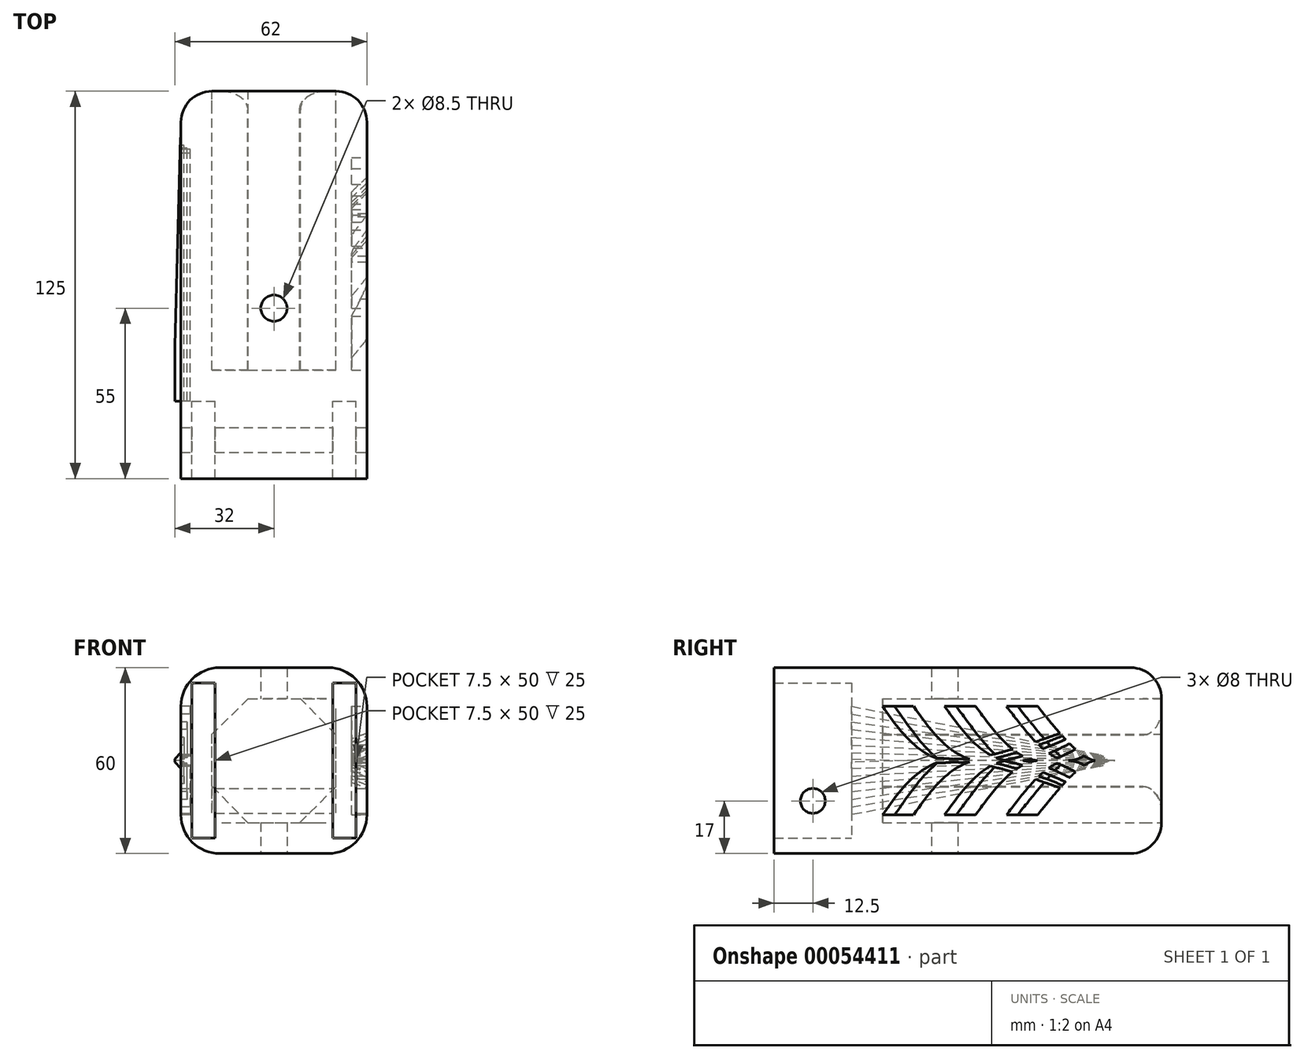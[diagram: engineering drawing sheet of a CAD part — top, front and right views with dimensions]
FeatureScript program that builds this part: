
annotation { "Feature Type Name" : "Feature", "Feature Type Description" : "" }
export const myFeature = defineFeature(function(context is Context, id is Id, definition is map)
    precondition{}
    {
        {
            var Q0;
            Q0=qCreatedBy(makeId("Front.planeOp"),FACE);
            var sketch = newSketch(context, id + "F0", { "sketchPlane" : qUnion([Q0])});
            skLineSegment(sketch, "E0.bottom", {"start": v(-30, 30) * mm, "end": v(30, 30) * mm});
            skLineSegment(sketch, "E0.top", {"start": v(-30, -30) * mm, "end": v(30, -30) * mm});
            skLineSegment(sketch, "E0.left", {"start": v(-30, 30) * mm, "end": v(-30, -30) * mm});
            skLineSegment(sketch, "E0.right", {"start": v(30, 30) * mm, "end": v(30, -30) * mm});
            skPoint(sketch, "E1", {"position": v(-26.5, -30) * mm});
            skPoint(sketch, "E2", {"position": v(-19, -30) * mm});
            skPoint(sketch, "E3", {"position": v(19, -30) * mm});
            skPoint(sketch, "E4", {"position": v(30, -25) * mm});
            skPoint(sketch, "E5", {"position": v(30, 25) * mm});
            skPoint(sketch, "E6", {"position": v(0, 30) * mm});
            skPoint(sketch, "E7", {"position": v(0, -30) * mm});
            skPoint(sketch, "E8", {"position": v(26.5, -30) * mm});
            skPoint(sketch, "E9", {"position": v(30, 0) * mm});
            skLineSegment(sketch, "E10", {"start": v(-26.5, -30) * mm, "end": v(-26.5, 30) * mm, "construction": true});
            skLineSegment(sketch, "E11", {"start": v(-19, -30) * mm, "end": v(-19, 30) * mm, "construction": true});
            skLineSegment(sketch, "E12", {"start": v(19, -30) * mm, "end": v(19, 30) * mm, "construction": true});
            skLineSegment(sketch, "E13", {"start": v(26.5, -30) * mm, "end": v(26.5, 30) * mm, "construction": true});
            skLineSegment(sketch, "E14", {"start": v(30, -25) * mm, "end": v(-30, -25) * mm, "construction": true});
            skLineSegment(sketch, "E15", {"start": v(30, 25) * mm, "end": v(-30, 25) * mm, "construction": true});
            skPoint(sketch, "E16", {"position": v(-26.5, 25) * mm});
            skPoint(sketch, "E17", {"position": v(-19, 25) * mm});
            skPoint(sketch, "E18", {"position": v(-26.5, -25) * mm});
            skPoint(sketch, "E19", {"position": v(-19, -25) * mm});
            skPoint(sketch, "E20", {"position": v(19, -25) * mm});
            skPoint(sketch, "E21", {"position": v(26.5, -25) * mm});
            skPoint(sketch, "E22", {"position": v(26.5, 25) * mm});
            skPoint(sketch, "E23", {"position": v(19, 25) * mm});
            skLineSegment(sketch, "E24", {"start": v(-26.5, 25) * mm, "end": v(-19, 25) * mm});
            skLineSegment(sketch, "E25", {"start": v(-26.5, 25) * mm, "end": v(-26.5, -25) * mm});
            skLineSegment(sketch, "E26", {"start": v(-26.5, -25) * mm, "end": v(-19, -25) * mm});
            skLineSegment(sketch, "E27", {"start": v(19, 25) * mm, "end": v(19, -25) * mm});
            skLineSegment(sketch, "E28", {"start": v(19, -25) * mm, "end": v(26.5, -25) * mm});
            skLineSegment(sketch, "E29", {"start": v(-19, 25) * mm, "end": v(-19, -25) * mm});
            skLineSegment(sketch, "E30", {"start": v(19, 25) * mm, "end": v(26.5, 25) * mm});
            skLineSegment(sketch, "E31", {"start": v(26.5, 25) * mm, "end": v(26.5, -25) * mm});
            skSolve(sketch);
        }
        {
            var Q0;
            Q0=makeQuery(id+"F0.imprint","IMPRINT",FACE,{"disambiguationData":[TD([[makeQuery(id+"F0.imprint","IMPRINT",EDGE,{"derivedFrom":sQuery(id+"F0.wireOp",EDGE,"E0.bottom")}),-1.0]])]});
            extrude(context, id + "F1", {"entities" : qUnion([Q0]), "depth" : 25 * mm});
        }
        {
            var Q0;
            Q0=makeQuery(id+"F1.opExtrude","SWEPT_FACE",FACE,{"disambiguationData":[OSD([sQuery(id+"F0.wireOp",EDGE,"E0.right")])]});
            var sketch = newSketch(context, id + "F2", { "sketchPlane" : qUnion([Q0])});
            skPoint(sketch, "E32", {"position": v(-12.5, -13) * mm});
            skSolve(sketch);
        }
        {
            var Q0;
            Q0=sQuery(id+"F2.wireOp",VERTEX,"E32");
            var Q1;
            Q1=makeQuery(id+"F1.opExtrude","SWEPT_BODY",BODY,{"disambiguationData":[OSD([sQuery(id+"F0.wireOp",EDGE,"E0.bottom"),sQuery(id+"F0.wireOp",EDGE,"E0.top"),sQuery(id+"F0.wireOp",EDGE,"E0.left"),sQuery(id+"F0.wireOp",EDGE,"E0.right"),sQuery(id+"F0.wireOp",EDGE,"E24"),sQuery(id+"F0.wireOp",EDGE,"E25"),sQuery(id+"F0.wireOp",EDGE,"E26"),sQuery(id+"F0.wireOp",EDGE,"E27"),sQuery(id+"F0.wireOp",EDGE,"E28"),sQuery(id+"F0.wireOp",EDGE,"E29"),sQuery(id+"F0.wireOp",EDGE,"E30"),sQuery(id+"F0.wireOp",EDGE,"E31")])]});
            hole(context, id + "F3", {"style" : HoleStyle.SIMPLE, "holeDiameter" : 8 * mm, "endStyle" : HoleEndStyle.THROUGH, "locations" : qUnion([Q0]), "scope" : qUnion([Q1])});
        }
        {
            var Q0;
            Q0=makeQuery(id+"F1.opExtrude","SWEPT_EDGE",EDGE,{"disambiguationData":[OSD([sQuery(id+"F0.wireOp",EDGE,"E0.bottom"),sQuery(id+"F0.wireOp",EDGE,"E0.left")])]});
            var Q1;
            Q1=makeQuery(id+"F1.opExtrude","SWEPT_EDGE",EDGE,{"disambiguationData":[OSD([sQuery(id+"F0.wireOp",EDGE,"E0.bottom"),sQuery(id+"F0.wireOp",EDGE,"E0.right")])]});
            var Q2;
            Q2=makeQuery(id+"F1.opExtrude","SWEPT_EDGE",EDGE,{"disambiguationData":[OSD([sQuery(id+"F0.wireOp",EDGE,"E0.top"),sQuery(id+"F0.wireOp",EDGE,"E0.left")])]});
            var Q3;
            Q3=makeQuery(id+"F1.opExtrude","SWEPT_EDGE",EDGE,{"disambiguationData":[OSD([sQuery(id+"F0.wireOp",EDGE,"E0.top"),sQuery(id+"F0.wireOp",EDGE,"E0.right")])]});
            fillet(context, id + "F4", {"entities" : qUnion([Q0, Q1, Q2, Q3]), "radius" : 12.5 * mm, "tangentPropagation" : true, "allowEdgeOverflow" : false});
        }
        {
            var Q0;
            Q0=makeQuery(id+"F1.opExtrude","CAP_FACE",FACE,{"disambiguationData":[OSD([sQuery(id+"F0.wireOp",EDGE,"E0.bottom"),sQuery(id+"F0.wireOp",EDGE,"E0.top"),sQuery(id+"F0.wireOp",EDGE,"E0.left"),sQuery(id+"F0.wireOp",EDGE,"E0.right"),sQuery(id+"F0.wireOp",EDGE,"E24"),sQuery(id+"F0.wireOp",EDGE,"E25"),sQuery(id+"F0.wireOp",EDGE,"E26"),sQuery(id+"F0.wireOp",EDGE,"E27"),sQuery(id+"F0.wireOp",EDGE,"E28"),sQuery(id+"F0.wireOp",EDGE,"E29"),sQuery(id+"F0.wireOp",EDGE,"E30"),sQuery(id+"F0.wireOp",EDGE,"E31")])],"isStart":true});
            var sketch = newSketch(context, id + "F5", { "sketchPlane" : qUnion([Q0])});
            skLineSegment(sketch, "E33.bottom", {"start": v(30, -30) * mm, "end": v(-30, -30) * mm});
            skLineSegment(sketch, "E33.top", {"start": v(30, 30) * mm, "end": v(-30, 30) * mm});
            skLineSegment(sketch, "E33.left", {"start": v(30, -30) * mm, "end": v(30, 30) * mm});
            skLineSegment(sketch, "E33.right", {"start": v(-30, -30) * mm, "end": v(-30, 30) * mm});
            skSolve(sketch);
        }
        {
            var Q0;
            Q0 = qSketchRegion(id + "F5", true);
            extrude(context, id + "F6", {"entities" : qUnion([Q0]), "operationType" : NewBodyOperationType.ADD, "depth" : 100 * mm});
        }
        {
            var Q0;
            Q0=makeQuery(id+"F6.opExtrude","SWEPT_EDGE",EDGE,{"disambiguationData":[OSD([sQuery(id+"F5.wireOp",EDGE,"E33.bottom"),sQuery(id+"F5.wireOp",EDGE,"E33.right")])]});
            var Q1;
            Q1=makeQuery(id+"F6.opExtrude","SWEPT_EDGE",EDGE,{"disambiguationData":[OSD([sQuery(id+"F5.wireOp",EDGE,"E33.bottom"),sQuery(id+"F5.wireOp",EDGE,"E33.left")])]});
            var Q2;
            Q2=makeQuery(id+"F6.opExtrude","SWEPT_EDGE",EDGE,{"disambiguationData":[OSD([sQuery(id+"F5.wireOp",EDGE,"E33.top"),sQuery(id+"F5.wireOp",EDGE,"E33.right")])]});
            var Q3;
            Q3=makeQuery(id+"F6.opExtrude","SWEPT_EDGE",EDGE,{"disambiguationData":[OSD([sQuery(id+"F5.wireOp",EDGE,"E33.top"),sQuery(id+"F5.wireOp",EDGE,"E33.left")])]});
            fillet(context, id + "F7", {"entities" : qUnion([Q0, Q1, Q2, Q3]), "radius" : 12.5 * mm, "tangentPropagation" : true, "allowEdgeOverflow" : false});
        }
        {
            var Q0;
            Q0=makeQuery(id+"F6.opExtrude","CAP_FACE",FACE,{"disambiguationData":[OSD([sQuery(id+"F5.wireOp",EDGE,"E33.bottom"),sQuery(id+"F5.wireOp",EDGE,"E33.top"),sQuery(id+"F5.wireOp",EDGE,"E33.left"),sQuery(id+"F5.wireOp",EDGE,"E33.right")])],"isStart":false});
            fillet(context, id + "F8", {"entities" : qUnion([Q0]), "radius" : 10 * mm, "tangentPropagation" : true, "allowEdgeOverflow" : false});
        }
        {
            var Q0;
            Q0=makeQuery(id+"F6.opExtrude","CAP_FACE",FACE,{"disambiguationData":[OSD([sQuery(id+"F5.wireOp",EDGE,"E33.bottom"),sQuery(id+"F5.wireOp",EDGE,"E33.top"),sQuery(id+"F5.wireOp",EDGE,"E33.left"),sQuery(id+"F5.wireOp",EDGE,"E33.right")])],"isStart":false});
            var sketch = newSketch(context, id + "F9", { "sketchPlane" : qUnion([Q0])});
            skPoint(sketch, "E34", {"position": v(0, 0) * mm});
            skCircle(sketch, "E35.cCircle", {"center": v(0, 0) * mm, "radius": 20.07 * mm, "construction": true});
            skLineSegment(sketch, "E35.0", {"start": v(-20.14, 8.14) * mm, "end": v(-8.49, 20) * mm});
            skLineSegment(sketch, "E35.1", {"start": v(-8.49, 20) * mm, "end": v(8.14, 20.14) * mm});
            skLineSegment(sketch, "E35.2", {"start": v(8.14, 20.14) * mm, "end": v(20, 8.49) * mm});
            skLineSegment(sketch, "E35.3", {"start": v(20, 8.49) * mm, "end": v(20.14, -8.14) * mm});
            skLineSegment(sketch, "E35.4", {"start": v(20.14, -8.14) * mm, "end": v(8.49, -20) * mm});
            skLineSegment(sketch, "E35.5", {"start": v(8.49, -20) * mm, "end": v(-8.14, -20.14) * mm});
            skLineSegment(sketch, "E35.6", {"start": v(-8.14, -20.14) * mm, "end": v(-20, -8.49) * mm});
            skLineSegment(sketch, "E35.7", {"start": v(-20, -8.49) * mm, "end": v(-20.14, 8.14) * mm});
            skPoint(sketch, "E35.0.midPoint", {"position": v(-14.31, 14.07) * mm});
            skSolve(sketch);
        }
        {
            var Q0;
            {var subQ1=sQuery(id+"F5.wireOp",EDGE,"E33.right");var subQ2=sQuery(id+"F5.wireOp",EDGE,"E33.left");var subQ3=sQuery(id+"F5.wireOp",EDGE,"E33.top");var subQ4=sQuery(id+"F5.wireOp",EDGE,"E33.bottom");var subQ5=makeQuery(id+"F6.opExtrude","CAP_FACE",FACE,{"disambiguationData":[OSD([subQ4,subQ3,subQ2,subQ1])],"isStart":false});var subQ15=makeQuery(id+"F8.opFillet","BLEND_EDGE",EDGE,{"blendedFrom":[makeQuery(id+"F6.opExtrude","CAP_EDGE",EDGE,{"disambiguationData":[OSD([subQ1])],"isStart":false}),subQ5],"blendedInto":[subQ5]});var subQ18=sQuery(id+"F9.wireOp",EDGE,"E35.0");var subQ20=makeQuery(id+"F9.imprint","INTERSECT",VERTEX,{"derivedFrom":[subQ15,subQ18]});Q0=makeQuery(id+"F9.imprint","IMPRINT",FACE,{"disambiguationData":[TD([[makeQuery(id+"F9.imprint","IMPRINT",EDGE,{"disambiguationData":[TD([[subQ20,-1.0]])],"derivedFrom":subQ18}),-1.0]])]});}
            extrude(context, id + "F10", {"entities" : qUnion([Q0]), "operationType" : NewBodyOperationType.REMOVE, "oppositeDirection" : true, "depth" : 90 * mm});
        }
        {
            var Q0;
            Q0=makeQuery(id+"F10.boolean.opBoolean","COPY",EDGE,{"derivedFrom":makeQuery(id+"F10.opExtrude","CAP_EDGE",EDGE,{"disambiguationData":[OSD([sQuery(id+"F9.wireOp",EDGE,"E35.2")])],"isStart":true})});
            var Q1;
            Q1=makeQuery(id+"F10.boolean.opBoolean","COPY",EDGE,{"derivedFrom":makeQuery(id+"F10.opExtrude","CAP_EDGE",EDGE,{"disambiguationData":[OSD([sQuery(id+"F9.wireOp",EDGE,"E35.4")])],"isStart":true})});
            var Q2;
            Q2=makeQuery(id+"F10.boolean.opBoolean","COPY",EDGE,{"derivedFrom":makeQuery(id+"F10.opExtrude","CAP_EDGE",EDGE,{"disambiguationData":[OSD([sQuery(id+"F9.wireOp",EDGE,"E35.0")])],"isStart":true})});
            var Q3;
            Q3=makeQuery(id+"F10.boolean.opBoolean","COPY",EDGE,{"derivedFrom":makeQuery(id+"F10.opExtrude","CAP_EDGE",EDGE,{"disambiguationData":[OSD([sQuery(id+"F9.wireOp",EDGE,"E35.6")])],"isStart":true})});
            fillet(context, id + "F11", {"entities" : qUnion([Q0, Q1, Q2, Q3]), "radius" : 6 * mm, "tangentPropagation" : true, "allowEdgeOverflow" : false});
        }
        {
            var Q0;
            Q0=makeQuery(id+"F6.boolean.opBoolean","MERGE",FACE,{"derivedFrom":[makeQuery(id+"F1.opExtrude","SWEPT_FACE",FACE,{"disambiguationData":[OSD([sQuery(id+"F0.wireOp",EDGE,"E0.right")])]}),makeQuery(id+"F6.opExtrude","SWEPT_FACE",FACE,{"disambiguationData":[OSD([sQuery(id+"F5.wireOp",EDGE,"E33.right")])]})]});
            var sketch = newSketch(context, id + "F12", { "sketchPlane" : qUnion([Q0])});
            skPoint(sketch, "E36", {"position": v(10, 17.5) * mm});
            skPoint(sketch, "E37", {"position": v(20, 17.5) * mm});
            skPoint(sketch, "E38", {"position": v(30, 17.5) * mm});
            skPoint(sketch, "E39", {"position": v(40, 17.5) * mm});
            skPoint(sketch, "E40", {"position": v(50, 17.5) * mm});
            skPoint(sketch, "E41", {"position": v(60, 17.5) * mm});
            skPoint(sketch, "E42", {"position": v(70, 17.5) * mm});
            skPoint(sketch, "E43", {"position": v(80, 17.5) * mm});
            skPoint(sketch, "E44", {"position": v(10, -17.5) * mm});
            skPoint(sketch, "E45", {"position": v(20, -17.5) * mm});
            skPoint(sketch, "E46", {"position": v(30, -17.5) * mm});
            skPoint(sketch, "E47", {"position": v(40, -17.5) * mm});
            skPoint(sketch, "E48", {"position": v(50, -17.5) * mm});
            skPoint(sketch, "E49", {"position": v(60, -17.5) * mm});
            skPoint(sketch, "E50", {"position": v(70, -17.5) * mm});
            skPoint(sketch, "E51", {"position": v(80, -17.5) * mm});
            skPoint(sketch, "E52", {"position": v(10, 0) * mm});
            skPoint(sketch, "E53", {"position": v(20, 0) * mm});
            skPoint(sketch, "E54", {"position": v(30, 0) * mm});
            skPoint(sketch, "E55", {"position": v(40, 0) * mm});
            skPoint(sketch, "E56", {"position": v(50, 0) * mm});
            skPoint(sketch, "E57", {"position": v(60, 0) * mm});
            skPoint(sketch, "E58", {"position": v(70, 0) * mm});
            skPoint(sketch, "E59", {"position": v(80, 0) * mm});
            skFitSpline(sketch, "E60", {"points": [v(0, 17.5) * mm, v(20, 0) * mm, v(90, 17.5) * mm], "startDerivative": vector(41.71, -60.4) * mm, "endDerivative": vector(131, 51.29) * mm});
            skFitSpline(sketch, "E61", {"points": [v(0, -17.5) * mm, v(20, 0) * mm, v(90, -17.5) * mm], "startDerivative": vector(41.71, 60.4) * mm, "endDerivative": vector(131, -51.29) * mm});
            skFitSpline(sketch, "E62", {"points": [v(10, 17.5) * mm, v(30, 0) * mm, v(90, 17.5) * mm], "startDerivative": vector(41.1, -58.8) * mm, "endDerivative": vector(113.79, 51.08) * mm});
            skFitSpline(sketch, "E63", {"points": [v(20, 17.5) * mm, v(40, 0) * mm, v(90, 17.5) * mm], "startDerivative": vector(40.53, -57.16) * mm, "endDerivative": vector(96.3, 51) * mm});
            skFitSpline(sketch, "E64", {"points": [v(30, 17.5) * mm, v(50, 0) * mm, v(90, 17.5) * mm], "startDerivative": vector(40.03, -55.5) * mm, "endDerivative": vector(78.39, 51.12) * mm});
            skFitSpline(sketch, "E65", {"points": [v(40, 17.5) * mm, v(60, 0) * mm, v(90, 17.5) * mm], "startDerivative": vector(39.74, -53.9) * mm, "endDerivative": vector(59.81, 51.56) * mm});
            skFitSpline(sketch, "E66", {"points": [v(50, 17.5) * mm, v(70, 0) * mm, v(90, 17.5) * mm], "startDerivative": vector(40, -52.5) * mm, "endDerivative": vector(40, 52.5) * mm});
            skFitSpline(sketch, "E67", {"points": [v(60, 17.5) * mm, v(80, 0) * mm, v(90, 17.5) * mm], "startDerivative": vector(41.68, -51.54) * mm, "endDerivative": vector(17.77, 53.96) * mm});
            skFitSpline(sketch, "E68", {"points": [v(10, -17.5) * mm, v(30, 0) * mm, v(90, -17.5) * mm], "startDerivative": vector(41.1, 58.8) * mm, "endDerivative": vector(113.79, -51.08) * mm});
            skFitSpline(sketch, "E69", {"points": [v(20, -17.5) * mm, v(40, 0) * mm, v(90, -17.5) * mm], "startDerivative": vector(40.53, 57.16) * mm, "endDerivative": vector(96.3, -51) * mm});
            skFitSpline(sketch, "E70", {"points": [v(30, -17.5) * mm, v(50, 0) * mm, v(90, -17.5) * mm], "startDerivative": vector(40.03, 55.5) * mm, "endDerivative": vector(78.39, -51.12) * mm});
            skFitSpline(sketch, "E71", {"points": [v(40, -17.5) * mm, v(60, 0) * mm, v(90, -17.5) * mm], "startDerivative": vector(39.74, 53.9) * mm, "endDerivative": vector(59.81, -51.56) * mm});
            skFitSpline(sketch, "E72", {"points": [v(50, -17.5) * mm, v(70, 0) * mm, v(90, -17.5) * mm], "startDerivative": vector(40, 52.5) * mm, "endDerivative": vector(40, -52.5) * mm});
            skFitSpline(sketch, "E73", {"points": [v(60, -17.5) * mm, v(80, 0) * mm, v(90, -17.5) * mm], "startDerivative": vector(41.68, 51.54) * mm, "endDerivative": vector(17.77, -53.96) * mm});
            skSolve(sketch);
        }
        {
            var Q0;
            {var subQ0=sQuery(id+"F12.wireOp",EDGE,"E72");var subQ1=sQuery(id+"F12.wireOp",EDGE,"E61");var subQ2=makeQuery(id+"F12.imprint","INTERSECT",VERTEX,{"derivedFrom":[subQ1,subQ0]});Q0=makeQuery(id+"F12.imprint","IMPRINT",FACE,{"disambiguationData":[TD([[makeQuery(id+"F12.imprint","IMPRINT",EDGE,{"disambiguationData":[TD([[subQ2,-1.0]])],"derivedFrom":subQ1}),-1.0]])]});}
            var Q1;
            {var subQ0=sQuery(id+"F12.wireOp",EDGE,"E70");var subQ1=sQuery(id+"F12.wireOp",EDGE,"E61");var subQ2=makeQuery(id+"F12.imprint","INTERSECT",VERTEX,{"derivedFrom":[subQ1,subQ0]});Q1=makeQuery(id+"F12.imprint","IMPRINT",FACE,{"disambiguationData":[TD([[makeQuery(id+"F12.imprint","IMPRINT",EDGE,{"disambiguationData":[TD([[subQ2,-1.0]])],"derivedFrom":subQ1}),-1.0]])]});}
            var Q2;
            {var subQ6=sQuery(id+"F12.wireOp",EDGE,"E60");var subQ8=sQuery(id+"F12.wireOp",EDGE,"E68");var subQ10=makeQuery(id+"F12.imprint","INTERSECT",VERTEX,{"disambiguationData":[OD(0.0)],"derivedFrom":[subQ6,subQ8]});Q2=makeQuery(id+"F12.imprint","IMPRINT",FACE,{"disambiguationData":[TD([[makeQuery(id+"F12.imprint","IMPRINT",EDGE,{"disambiguationData":[TD([[subQ10,-1.0]])],"derivedFrom":subQ6}),-1.0]])]});}
            var Q3;
            {var subQ1=sQuery(id+"F12.wireOp",EDGE,"E61");var subQ5=sQuery(id+"F12.wireOp",EDGE,"E62");var subQ9=makeQuery(id+"F12.imprint","INTERSECT",VERTEX,{"disambiguationData":[OD(0.0)],"derivedFrom":[subQ1,subQ5]});Q3=makeQuery(id+"F12.imprint","IMPRINT",FACE,{"disambiguationData":[TD([[makeQuery(id+"F12.imprint","IMPRINT",EDGE,{"disambiguationData":[TD([[subQ9,-1.0]])],"derivedFrom":subQ1}),1.0]])]});}
            var Q4;
            {var subQ0=sQuery(id+"F12.wireOp",EDGE,"E64");var subQ1=sQuery(id+"F12.wireOp",EDGE,"E60");var subQ2=makeQuery(id+"F12.imprint","INTERSECT",VERTEX,{"derivedFrom":[subQ1,subQ0]});Q4=makeQuery(id+"F12.imprint","IMPRINT",FACE,{"disambiguationData":[TD([[makeQuery(id+"F12.imprint","IMPRINT",EDGE,{"disambiguationData":[TD([[subQ2,-1.0]])],"derivedFrom":subQ1}),1.0]])]});}
            var Q5;
            {var subQ0=sQuery(id+"F12.wireOp",EDGE,"E66");var subQ1=sQuery(id+"F12.wireOp",EDGE,"E60");var subQ2=makeQuery(id+"F12.imprint","INTERSECT",VERTEX,{"derivedFrom":[subQ1,subQ0]});Q5=makeQuery(id+"F12.imprint","IMPRINT",FACE,{"disambiguationData":[TD([[makeQuery(id+"F12.imprint","IMPRINT",EDGE,{"disambiguationData":[TD([[subQ2,-1.0]])],"derivedFrom":subQ1}),1.0]])]});}
            var Q6;
            {var subQ0=sQuery(id+"F12.wireOp",EDGE,"E64");var subQ1=sQuery(id+"F12.wireOp",EDGE,"E62");var subQ2=makeQuery(id+"F12.imprint","INTERSECT",VERTEX,{"derivedFrom":[subQ1,subQ0]});Q6=makeQuery(id+"F12.imprint","IMPRINT",FACE,{"disambiguationData":[TD([[makeQuery(id+"F12.imprint","IMPRINT",EDGE,{"disambiguationData":[TD([[subQ2,-1.0]])],"derivedFrom":subQ1}),-1.0]])]});}
            var Q7;
            {var subQ0=sQuery(id+"F12.wireOp",EDGE,"E70");var subQ1=sQuery(id+"F12.wireOp",EDGE,"E68");var subQ2=makeQuery(id+"F12.imprint","INTERSECT",VERTEX,{"derivedFrom":[subQ1,subQ0]});Q7=makeQuery(id+"F12.imprint","IMPRINT",FACE,{"disambiguationData":[TD([[makeQuery(id+"F12.imprint","IMPRINT",EDGE,{"disambiguationData":[TD([[subQ2,-1.0]])],"derivedFrom":subQ1}),1.0]])]});}
            var Q8;
            {var subQ0=sQuery(id+"F12.wireOp",EDGE,"E66");var subQ1=sQuery(id+"F12.wireOp",EDGE,"E62");var subQ2=makeQuery(id+"F12.imprint","INTERSECT",VERTEX,{"derivedFrom":[subQ1,subQ0]});Q8=makeQuery(id+"F12.imprint","IMPRINT",FACE,{"disambiguationData":[TD([[makeQuery(id+"F12.imprint","IMPRINT",EDGE,{"disambiguationData":[TD([[subQ2,-1.0]])],"derivedFrom":subQ1}),-1.0]])]});}
            var Q9;
            {var subQ0=sQuery(id+"F12.wireOp",EDGE,"E66");var subQ1=sQuery(id+"F12.wireOp",EDGE,"E64");var subQ2=makeQuery(id+"F12.imprint","INTERSECT",VERTEX,{"derivedFrom":[subQ1,subQ0]});Q9=makeQuery(id+"F12.imprint","IMPRINT",FACE,{"disambiguationData":[TD([[makeQuery(id+"F12.imprint","IMPRINT",EDGE,{"disambiguationData":[TD([[subQ2,-1.0]])],"derivedFrom":subQ1}),-1.0]])]});}
            var Q10;
            {var subQ0=sQuery(id+"F12.wireOp",EDGE,"E72");var subQ1=sQuery(id+"F12.wireOp",EDGE,"E68");var subQ2=makeQuery(id+"F12.imprint","INTERSECT",VERTEX,{"derivedFrom":[subQ1,subQ0]});Q10=makeQuery(id+"F12.imprint","IMPRINT",FACE,{"disambiguationData":[TD([[makeQuery(id+"F12.imprint","IMPRINT",EDGE,{"disambiguationData":[TD([[subQ2,-1.0]])],"derivedFrom":subQ1}),1.0]])]});}
            var Q11;
            {var subQ0=sQuery(id+"F12.wireOp",EDGE,"E72");var subQ1=sQuery(id+"F12.wireOp",EDGE,"E70");var subQ2=makeQuery(id+"F12.imprint","INTERSECT",VERTEX,{"derivedFrom":[subQ1,subQ0]});Q11=makeQuery(id+"F12.imprint","IMPRINT",FACE,{"disambiguationData":[TD([[makeQuery(id+"F12.imprint","IMPRINT",EDGE,{"disambiguationData":[TD([[subQ2,-1.0]])],"derivedFrom":subQ1}),1.0]])]});}
            var Q12;
            {var subQ0=sQuery(id+"F12.wireOp",EDGE,"E70");var subQ1=sQuery(id+"F12.wireOp",EDGE,"E64");var subQ2=makeQuery(id+"F12.imprint","INTERSECT",VERTEX,{"disambiguationData":[OD(1.0)],"derivedFrom":[subQ1,subQ0]});Q12=makeQuery(id+"F12.imprint","IMPRINT",FACE,{"disambiguationData":[TD([[makeQuery(id+"F12.imprint","IMPRINT",EDGE,{"disambiguationData":[TD([[subQ2,-1.0]])],"derivedFrom":subQ1}),-1.0]])]});}
            var Q13;
            {var subQ0=sQuery(id+"F12.wireOp",EDGE,"E72");var subQ1=sQuery(id+"F12.wireOp",EDGE,"E66");var subQ2=makeQuery(id+"F12.imprint","INTERSECT",VERTEX,{"derivedFrom":[subQ1,subQ0]});Q13=makeQuery(id+"F12.imprint","IMPRINT",FACE,{"disambiguationData":[TD([[makeQuery(id+"F12.imprint","IMPRINT",EDGE,{"disambiguationData":[TD([[subQ2,-1.0]])],"derivedFrom":subQ1}),-1.0]])]});}
            extrude(context, id + "F13", {"entities" : qUnion([Q0, Q1, Q2, Q3, Q4, Q5, Q6, Q7, Q8, Q9, Q10, Q11, Q12, Q13]), "operationType" : NewBodyOperationType.REMOVE, "oppositeDirection" : true, "depth" : 5 * mm});
        }
        {
            var Q0;
            Q0=makeQuery(id+"F6.boolean.opBoolean","MERGE",FACE,{"derivedFrom":[makeQuery(id+"F1.opExtrude","SWEPT_FACE",FACE,{"disambiguationData":[OSD([sQuery(id+"F0.wireOp",EDGE,"E0.top")])]}),makeQuery(id+"F6.opExtrude","SWEPT_FACE",FACE,{"disambiguationData":[OSD([sQuery(id+"F5.wireOp",EDGE,"E33.bottom")])]})]});
            var sketch = newSketch(context, id + "F14", { "sketchPlane" : qUnion([Q0])});
            skPoint(sketch, "E74", {"position": v(0, -90) * mm});
            skPoint(sketch, "E75", {"position": v(0, -30) * mm});
            skSolve(sketch);
        }
        {
            var Q0;
            Q0=sQuery(id+"F14.wireOp",VERTEX,"E75");
            var Q1;
            Q1=makeQuery(id+"F1.opExtrude","SWEPT_BODY",BODY,{"disambiguationData":[OSD([sQuery(id+"F0.wireOp",EDGE,"E0.bottom"),sQuery(id+"F0.wireOp",EDGE,"E0.top"),sQuery(id+"F0.wireOp",EDGE,"E0.left"),sQuery(id+"F0.wireOp",EDGE,"E0.right"),sQuery(id+"F0.wireOp",EDGE,"E24"),sQuery(id+"F0.wireOp",EDGE,"E25"),sQuery(id+"F0.wireOp",EDGE,"E26"),sQuery(id+"F0.wireOp",EDGE,"E27"),sQuery(id+"F0.wireOp",EDGE,"E28"),sQuery(id+"F0.wireOp",EDGE,"E29"),sQuery(id+"F0.wireOp",EDGE,"E30"),sQuery(id+"F0.wireOp",EDGE,"E31")])]});
            hole(context, id + "F15", {"style" : HoleStyle.SIMPLE, "holeDiameter" : 8.5 * mm, "endStyle" : HoleEndStyle.THROUGH, "locations" : qUnion([Q0]), "scope" : qUnion([Q1])});
        }
        {
            var Q0;
            {var subQ0=sQuery(id+"F12.wireOp",EDGE,"E67");Q0=makeQuery(id+"F13.boolean.opBoolean","COPY",EDGE,{"derivedFrom":makeQuery(id+"F13.opExtrude","CAP_EDGE",EDGE,{"disambiguationData":[OSD([subQ0]),TDD([makeQuery(id+"F12.imprint","IMPRINT",EDGE,{"disambiguationData":[TD([[makeQuery(id+"F12.imprint","INTERSECT",VERTEX,{"derivedFrom":[sQuery(id+"F12.wireOp",EDGE,"E60"),subQ0]}),1.0]])],"derivedFrom":subQ0})])],"isStart":false})});}
            var Q1;
            {var subQ0=sQuery(id+"F12.wireOp",EDGE,"E67");Q1=makeQuery(id+"F13.boolean.opBoolean","COPY",EDGE,{"derivedFrom":makeQuery(id+"F13.opExtrude","CAP_EDGE",EDGE,{"disambiguationData":[OSD([subQ0]),TDD([makeQuery(id+"F12.imprint","IMPRINT",EDGE,{"disambiguationData":[TD([[makeQuery(id+"F12.imprint","INTERSECT",VERTEX,{"derivedFrom":[sQuery(id+"F12.wireOp",EDGE,"E62"),subQ0]}),-1.0]])],"derivedFrom":subQ0})])],"isStart":false})});}
            var Q2;
            {var subQ0=sQuery(id+"F12.wireOp",EDGE,"E67");Q2=makeQuery(id+"F13.boolean.opBoolean","COPY",EDGE,{"derivedFrom":makeQuery(id+"F13.opExtrude","CAP_EDGE",EDGE,{"disambiguationData":[OSD([subQ0]),TDD([makeQuery(id+"F12.imprint","IMPRINT",EDGE,{"disambiguationData":[TD([[makeQuery(id+"F12.imprint","INTERSECT",VERTEX,{"derivedFrom":[sQuery(id+"F12.wireOp",EDGE,"E64"),subQ0]}),-1.0]])],"derivedFrom":subQ0})])],"isStart":false})});}
            var Q3;
            {var subQ0=sQuery(id+"F12.wireOp",EDGE,"E65");Q3=makeQuery(id+"F13.boolean.opBoolean","COPY",EDGE,{"derivedFrom":makeQuery(id+"F13.opExtrude","CAP_EDGE",EDGE,{"disambiguationData":[OSD([subQ0]),TDD([makeQuery(id+"F12.imprint","IMPRINT",EDGE,{"disambiguationData":[TD([[makeQuery(id+"F12.imprint","INTERSECT",VERTEX,{"derivedFrom":[sQuery(id+"F12.wireOp",EDGE,"E62"),subQ0]}),-1.0]])],"derivedFrom":subQ0})])],"isStart":false})});}
            var Q4;
            {var subQ0=sQuery(id+"F12.wireOp",EDGE,"E65");Q4=makeQuery(id+"F13.boolean.opBoolean","COPY",EDGE,{"derivedFrom":makeQuery(id+"F13.opExtrude","CAP_EDGE",EDGE,{"disambiguationData":[OSD([subQ0]),TDD([makeQuery(id+"F12.imprint","IMPRINT",EDGE,{"disambiguationData":[TD([[makeQuery(id+"F12.imprint","INTERSECT",VERTEX,{"derivedFrom":[sQuery(id+"F12.wireOp",EDGE,"E60"),subQ0]}),1.0]])],"derivedFrom":subQ0})])],"isStart":false})});}
            var Q5;
            {var subQ0=sQuery(id+"F12.wireOp",EDGE,"E73");Q5=makeQuery(id+"F13.boolean.opBoolean","COPY",EDGE,{"derivedFrom":makeQuery(id+"F13.opExtrude","CAP_EDGE",EDGE,{"disambiguationData":[OSD([subQ0]),TDD([makeQuery(id+"F12.imprint","IMPRINT",EDGE,{"disambiguationData":[TD([[makeQuery(id+"F12.imprint","INTERSECT",VERTEX,{"derivedFrom":[sQuery(id+"F12.wireOp",EDGE,"E70"),subQ0]}),-1.0]])],"derivedFrom":subQ0})])],"isStart":false})});}
            var Q6;
            {var subQ0=sQuery(id+"F12.wireOp",EDGE,"E73");Q6=makeQuery(id+"F13.boolean.opBoolean","COPY",EDGE,{"derivedFrom":makeQuery(id+"F13.opExtrude","CAP_EDGE",EDGE,{"disambiguationData":[OSD([subQ0]),TDD([makeQuery(id+"F12.imprint","IMPRINT",EDGE,{"disambiguationData":[TD([[makeQuery(id+"F12.imprint","INTERSECT",VERTEX,{"derivedFrom":[sQuery(id+"F12.wireOp",EDGE,"E68"),subQ0]}),-1.0]])],"derivedFrom":subQ0})])],"isStart":false})});}
            var Q7;
            {var subQ0=sQuery(id+"F12.wireOp",EDGE,"E71");Q7=makeQuery(id+"F13.boolean.opBoolean","COPY",EDGE,{"derivedFrom":makeQuery(id+"F13.opExtrude","CAP_EDGE",EDGE,{"disambiguationData":[OSD([subQ0]),TDD([makeQuery(id+"F12.imprint","IMPRINT",EDGE,{"disambiguationData":[TD([[makeQuery(id+"F12.imprint","INTERSECT",VERTEX,{"derivedFrom":[sQuery(id+"F12.wireOp",EDGE,"E68"),subQ0]}),-1.0]])],"derivedFrom":subQ0})])],"isStart":false})});}
            var Q8;
            {var subQ0=sQuery(id+"F12.wireOp",EDGE,"E73");Q8=makeQuery(id+"F13.boolean.opBoolean","COPY",EDGE,{"derivedFrom":makeQuery(id+"F13.opExtrude","CAP_EDGE",EDGE,{"disambiguationData":[OSD([subQ0]),TDD([makeQuery(id+"F12.imprint","IMPRINT",EDGE,{"disambiguationData":[TD([[makeQuery(id+"F12.imprint","INTERSECT",VERTEX,{"derivedFrom":[sQuery(id+"F12.wireOp",EDGE,"E61"),subQ0]}),1.0]])],"derivedFrom":subQ0})])],"isStart":false})});}
            var Q9;
            {var subQ0=sQuery(id+"F12.wireOp",EDGE,"E71");Q9=makeQuery(id+"F13.boolean.opBoolean","COPY",EDGE,{"derivedFrom":makeQuery(id+"F13.opExtrude","CAP_EDGE",EDGE,{"disambiguationData":[OSD([subQ0]),TDD([makeQuery(id+"F12.imprint","IMPRINT",EDGE,{"disambiguationData":[TD([[makeQuery(id+"F12.imprint","INTERSECT",VERTEX,{"derivedFrom":[sQuery(id+"F12.wireOp",EDGE,"E61"),subQ0]}),1.0]])],"derivedFrom":subQ0})])],"isStart":false})});}
            var Q10;
            {var subQ0=sQuery(id+"F12.wireOp",EDGE,"E63");Q10=makeQuery(id+"F13.boolean.opBoolean","COPY",EDGE,{"derivedFrom":makeQuery(id+"F13.opExtrude","CAP_EDGE",EDGE,{"disambiguationData":[OSD([subQ0]),TDD([makeQuery(id+"F12.imprint","IMPRINT",EDGE,{"disambiguationData":[TD([[makeQuery(id+"F12.imprint","INTERSECT",VERTEX,{"disambiguationData":[OD(0.0)],"derivedFrom":[subQ0,sQuery(id+"F12.wireOp",EDGE,"E68")]}),1.0]])],"derivedFrom":subQ0})])],"isStart":false})});}
            var Q11;
            {var subQ0=sQuery(id+"F12.wireOp",EDGE,"E69");Q11=makeQuery(id+"F13.boolean.opBoolean","COPY",EDGE,{"derivedFrom":makeQuery(id+"F13.opExtrude","CAP_EDGE",EDGE,{"disambiguationData":[OSD([subQ0]),TDD([makeQuery(id+"F12.imprint","IMPRINT",EDGE,{"disambiguationData":[TD([[makeQuery(id+"F12.imprint","INTERSECT",VERTEX,{"disambiguationData":[OD(0.0)],"derivedFrom":[sQuery(id+"F12.wireOp",EDGE,"E62"),subQ0]}),1.0]])],"derivedFrom":subQ0})])],"isStart":false})});}
            chamfer(context, id + "F16", {"entities" : qUnion([Q0, Q1, Q2, Q3, Q4, Q5, Q6, Q7, Q8, Q9, Q10, Q11]), "width" : 5 * mm, "tangentPropagation" : true});
        }
        {
            var Q0;
            Q0=makeQuery(id+"F6.boolean.opBoolean","MERGE",FACE,{"derivedFrom":[makeQuery(id+"F1.opExtrude","SWEPT_FACE",FACE,{"disambiguationData":[OSD([sQuery(id+"F0.wireOp",EDGE,"E0.left")])]}),makeQuery(id+"F6.opExtrude","SWEPT_FACE",FACE,{"disambiguationData":[OSD([sQuery(id+"F5.wireOp",EDGE,"E33.left")])]})]});
            var sketch = newSketch(context, id + "F17", { "sketchPlane" : qUnion([Q0])});
            skPoint(sketch, "E76", {"position": v(-90, 0) * mm});
            skPoint(sketch, "E77", {"position": v(0, 17.5) * mm});
            skPoint(sketch, "E78", {"position": v(0, 12.5) * mm});
            skPoint(sketch, "E79", {"position": v(0, 7.5) * mm});
            skPoint(sketch, "E80", {"position": v(0, 2.5) * mm});
            skPoint(sketch, "E81", {"position": v(0, -2.5) * mm});
            skPoint(sketch, "E82", {"position": v(0, -7.5) * mm});
            skPoint(sketch, "E83", {"position": v(0, -12.5) * mm});
            skPoint(sketch, "E84", {"position": v(0, -17.5) * mm});
            skPoint(sketch, "E85", {"position": v(0, 15) * mm});
            skPoint(sketch, "E86", {"position": v(0, 10) * mm});
            skPoint(sketch, "E87", {"position": v(0, 5) * mm});
            skPoint(sketch, "E88", {"position": v(0, -5) * mm});
            skPoint(sketch, "E89", {"position": v(0, -10) * mm});
            skPoint(sketch, "E90", {"position": v(0, -15) * mm});
            skPoint(sketch, "E91", {"position": v(0, 0) * mm});
            skLineSegment(sketch, "E92", {"start": v(-90, 0) * mm, "end": v(0, -17.5) * mm, "construction": true});
            skLineSegment(sketch, "E93", {"start": v(0, -15) * mm, "end": v(-90, 0) * mm, "construction": true});
            skLineSegment(sketch, "E94", {"start": v(0, -12.5) * mm, "end": v(-90, 0) * mm, "construction": true});
            skLineSegment(sketch, "E95", {"start": v(0, -10) * mm, "end": v(-90, 0) * mm, "construction": true});
            skLineSegment(sketch, "E96", {"start": v(0, -7.5) * mm, "end": v(-90, 0) * mm, "construction": true});
            skLineSegment(sketch, "E97", {"start": v(0, -5) * mm, "end": v(-90, 0) * mm, "construction": true});
            skLineSegment(sketch, "E98", {"start": v(0, -2.5) * mm, "end": v(-90, 0) * mm, "construction": true});
            skLineSegment(sketch, "E99", {"start": v(0, 0) * mm, "end": v(-90, 0) * mm, "construction": true});
            skLineSegment(sketch, "E100", {"start": v(0, 2.5) * mm, "end": v(-90, 0) * mm, "construction": true});
            skLineSegment(sketch, "E101", {"start": v(0, 5) * mm, "end": v(-90, 0) * mm, "construction": true});
            skLineSegment(sketch, "E102", {"start": v(0, 7.5) * mm, "end": v(-90, 0) * mm, "construction": true});
            skLineSegment(sketch, "E103", {"start": v(0, 10) * mm, "end": v(-90, 0) * mm, "construction": true});
            skLineSegment(sketch, "E104", {"start": v(0, 12.5) * mm, "end": v(-90, 0) * mm, "construction": true});
            skLineSegment(sketch, "E105", {"start": v(0, 15) * mm, "end": v(-90, 0) * mm, "construction": true});
            skLineSegment(sketch, "E106", {"start": v(0, 17.5) * mm, "end": v(-90, 0) * mm, "construction": true});
            skLineSegment(sketch, "E107", {"start": v(0, 0) * mm, "end": v(0, -2.5) * mm});
            skLineSegment(sketch, "E108", {"start": v(0, -5) * mm, "end": v(0, -7.5) * mm});
            skLineSegment(sketch, "E109", {"start": v(0, -10) * mm, "end": v(0, -12.5) * mm});
            skLineSegment(sketch, "E110", {"start": v(0, -15) * mm, "end": v(0, -17.5) * mm});
            skLineSegment(sketch, "E111", {"start": v(0, 0) * mm, "end": v(0, 2.5) * mm});
            skLineSegment(sketch, "E112", {"start": v(0, 5) * mm, "end": v(0, 7.5) * mm});
            skLineSegment(sketch, "E113", {"start": v(0, 10) * mm, "end": v(0, 12.5) * mm});
            skLineSegment(sketch, "E114", {"start": v(0, 15) * mm, "end": v(0, 17.5) * mm});
            skPoint(sketch, "E115", {"position": v(-80, 1.94) * mm});
            skPoint(sketch, "E116", {"position": v(-80, -1.94) * mm});
            skPoint(sketch, "E117", {"position": v(-80, 1.67) * mm});
            skPoint(sketch, "E118", {"position": v(-80, 1.39) * mm});
            skPoint(sketch, "E119", {"position": v(-80, 1.11) * mm});
            skPoint(sketch, "E120", {"position": v(-80, 0.83) * mm});
            skPoint(sketch, "E121", {"position": v(-80, 0.56) * mm});
            skPoint(sketch, "E122", {"position": v(-80, 0.28) * mm});
            skPoint(sketch, "E123", {"position": v(-80, 0) * mm});
            skPoint(sketch, "E124", {"position": v(-80, -0.28) * mm});
            skPoint(sketch, "E125", {"position": v(-80, -0.56) * mm});
            skPoint(sketch, "E126", {"position": v(-80, -0.83) * mm});
            skPoint(sketch, "E127", {"position": v(-80, -1.11) * mm});
            skPoint(sketch, "E128", {"position": v(-80, -1.39) * mm});
            skPoint(sketch, "E129", {"position": v(-80, -1.67) * mm});
            skPoint(sketch, "E130", {"position": v(-85, 0) * mm});
            skLineSegment(sketch, "E131", {"start": v(-80, 1.94) * mm, "end": v(-85, 0) * mm});
            skLineSegment(sketch, "E132", {"start": v(-80, 1.67) * mm, "end": v(-85, 0) * mm});
            skLineSegment(sketch, "E133", {"start": v(-80, 1.39) * mm, "end": v(-85, 0) * mm});
            skLineSegment(sketch, "E134", {"start": v(-85, 0) * mm, "end": v(-80, 1.11) * mm});
            skLineSegment(sketch, "E135", {"start": v(-80, 0.83) * mm, "end": v(-85, 0) * mm});
            skLineSegment(sketch, "E136", {"start": v(-80, 0.56) * mm, "end": v(-85, 0) * mm});
            skLineSegment(sketch, "E137", {"start": v(-80, 0.28) * mm, "end": v(-85, 0) * mm});
            skLineSegment(sketch, "E138", {"start": v(-80, 0) * mm, "end": v(-85, 0) * mm});
            skLineSegment(sketch, "E139", {"start": v(-80, -0.28) * mm, "end": v(-85, 0) * mm});
            skLineSegment(sketch, "E140", {"start": v(-80, -0.56) * mm, "end": v(-85, 0) * mm});
            skLineSegment(sketch, "E141", {"start": v(-80, -0.83) * mm, "end": v(-85, 0) * mm});
            skLineSegment(sketch, "E142", {"start": v(-80, -1.11) * mm, "end": v(-85, 0) * mm});
            skLineSegment(sketch, "E143", {"start": v(-80, -1.39) * mm, "end": v(-85, 0) * mm});
            skLineSegment(sketch, "E144", {"start": v(-80, -1.67) * mm, "end": v(-85, 0) * mm});
            skLineSegment(sketch, "E145", {"start": v(-80, -1.94) * mm, "end": v(-85, 0) * mm});
            skLineSegment(sketch, "E146", {"start": v(0, 17.5) * mm, "end": v(-80, 1.94) * mm, "construction": true});
            skLineSegment(sketch, "E147", {"start": v(-80, -1.94) * mm, "end": v(0, -17.5) * mm});
            skLineSegment(sketch, "E148", {"start": v(0, -15) * mm, "end": v(-81.25, -1.46) * mm});
            skLineSegment(sketch, "E149", {"start": v(0, -12.5) * mm, "end": v(-81.43, -1.2) * mm});
            skLineSegment(sketch, "E150", {"start": v(0, -10) * mm, "end": v(-81.67, -0.93) * mm});
            skLineSegment(sketch, "E151", {"start": v(0, -7.5) * mm, "end": v(-82, -0.67) * mm});
            skLineSegment(sketch, "E152", {"start": v(0, -5) * mm, "end": v(-82.5, -0.42) * mm});
            skLineSegment(sketch, "E153", {"start": v(0, -2.5) * mm, "end": v(-83.33, -0.19) * mm});
            skLineSegment(sketch, "E154", {"start": v(0, 2.5) * mm, "end": v(-83.33, 0.19) * mm});
            skLineSegment(sketch, "E155", {"start": v(0, 5) * mm, "end": v(-83.33, 0.37) * mm});
            skLineSegment(sketch, "E156", {"start": v(0, 7.5) * mm, "end": v(-82, 0.67) * mm});
            skLineSegment(sketch, "E157", {"start": v(0, 10) * mm, "end": v(-81.67, 0.93) * mm});
            skLineSegment(sketch, "E158", {"start": v(0, 12.5) * mm, "end": v(-81.43, 1.2) * mm});
            skLineSegment(sketch, "E159", {"start": v(0, 15) * mm, "end": v(-81.25, 1.46) * mm});
            skLineSegment(sketch, "E160", {"start": v(0, 17.5) * mm, "end": v(-80, 1.94) * mm});
            skLineSegment(sketch, "E161", {"start": v(0, 0) * mm, "end": v(-85, 0) * mm});
            skSolve(sketch);
        }
        {
            var Q0;
            {var subQ1=sQuery(id+"F17.wireOp",EDGE,"E110");Q0=makeQuery(id+"F17.imprint","IMPRINT",FACE,{"disambiguationData":[TD([[makeQuery(id+"F17.imprint","IMPRINT",EDGE,{"derivedFrom":subQ1}),-1.0]])]});}
            var Q1;
            {var subQ4=sQuery(id+"F17.wireOp",EDGE,"E114");Q1=makeQuery(id+"F17.imprint","IMPRINT",FACE,{"disambiguationData":[TD([[makeQuery(id+"F17.imprint","IMPRINT",EDGE,{"derivedFrom":subQ4}),1.0]])]});}
            extrude(context, id + "F18", {"entities" : qUnion([Q0, Q1]), "operationType" : NewBodyOperationType.REMOVE, "oppositeDirection" : true, "depth" : 3 * mm});
        }
        {
            var Q0;
            {var subQ1=sQuery(id+"F17.wireOp",EDGE,"E109");Q0=makeQuery(id+"F17.imprint","IMPRINT",FACE,{"disambiguationData":[TD([[makeQuery(id+"F17.imprint","IMPRINT",EDGE,{"derivedFrom":subQ1}),-1.0]])]});}
            var Q1;
            {var subQ4=sQuery(id+"F17.wireOp",EDGE,"E113");Q1=makeQuery(id+"F17.imprint","IMPRINT",FACE,{"disambiguationData":[TD([[makeQuery(id+"F17.imprint","IMPRINT",EDGE,{"derivedFrom":subQ4}),1.0]])]});}
            extrude(context, id + "F19", {"entities" : qUnion([Q0, Q1]), "operationType" : NewBodyOperationType.REMOVE, "oppositeDirection" : true, "depth" : 2 * mm});
        }
        {
            var Q0;
            {var subQ1=sQuery(id+"F17.wireOp",EDGE,"E108");Q0=makeQuery(id+"F17.imprint","IMPRINT",FACE,{"disambiguationData":[TD([[makeQuery(id+"F17.imprint","IMPRINT",EDGE,{"derivedFrom":subQ1}),-1.0]])]});}
            var Q1;
            {var subQ4=sQuery(id+"F17.wireOp",EDGE,"E112");Q1=makeQuery(id+"F17.imprint","IMPRINT",FACE,{"disambiguationData":[TD([[makeQuery(id+"F17.imprint","IMPRINT",EDGE,{"derivedFrom":subQ4}),1.0]])]});}
            extrude(context, id + "F20", {"entities" : qUnion([Q0, Q1]), "operationType" : NewBodyOperationType.REMOVE, "depth" : 1 * mm});
        }
        {
            var Q0;
            {var subQ1=sQuery(id+"F17.wireOp",EDGE,"E108");Q0=makeQuery(id+"F17.imprint","IMPRINT",FACE,{"disambiguationData":[TD([[makeQuery(id+"F17.imprint","IMPRINT",EDGE,{"derivedFrom":subQ1}),-1.0]])]});}
            var Q1;
            {var subQ4=sQuery(id+"F17.wireOp",EDGE,"E112");Q1=makeQuery(id+"F17.imprint","IMPRINT",FACE,{"disambiguationData":[TD([[makeQuery(id+"F17.imprint","IMPRINT",EDGE,{"derivedFrom":subQ4}),1.0]])]});}
            extrude(context, id + "F21", {"entities" : qUnion([Q0, Q1]), "operationType" : NewBodyOperationType.REMOVE, "oppositeDirection" : true, "depth" : 1 * mm});
        }
        {
            var Q0;
            {var subQ1=sQuery(id+"F17.wireOp",EDGE,"E107");Q0=makeQuery(id+"F17.imprint","IMPRINT",FACE,{"disambiguationData":[TD([[makeQuery(id+"F17.imprint","IMPRINT",EDGE,{"derivedFrom":subQ1}),-1.0]])]});}
            var Q1;
            {var subQ1=sQuery(id+"F17.wireOp",EDGE,"E111");Q1=makeQuery(id+"F17.imprint","IMPRINT",FACE,{"disambiguationData":[TD([[makeQuery(id+"F17.imprint","IMPRINT",EDGE,{"derivedFrom":subQ1}),1.0]])]});}
            extrude(context, id + "F22", {"entities" : qUnion([Q0, Q1]), "operationType" : NewBodyOperationType.ADD, "depth" : 2 * mm});
        }
        {
            var Q0;
            Q0=makeQuery(id+"F22.opExtrude","CAP_EDGE",EDGE,{"disambiguationData":[OSD([sQuery(id+"F17.wireOp",EDGE,"E153")])],"isStart":false});
            var Q1;
            Q1=makeQuery(id+"F22.opExtrude","CAP_EDGE",EDGE,{"disambiguationData":[OSD([sQuery(id+"F17.wireOp",EDGE,"E154")])],"isStart":false});
            chamfer(context, id + "F23", {"entities" : qUnion([Q0, Q1]), "width" : 2 * mm, "tangentPropagation" : true});
        }
    });
